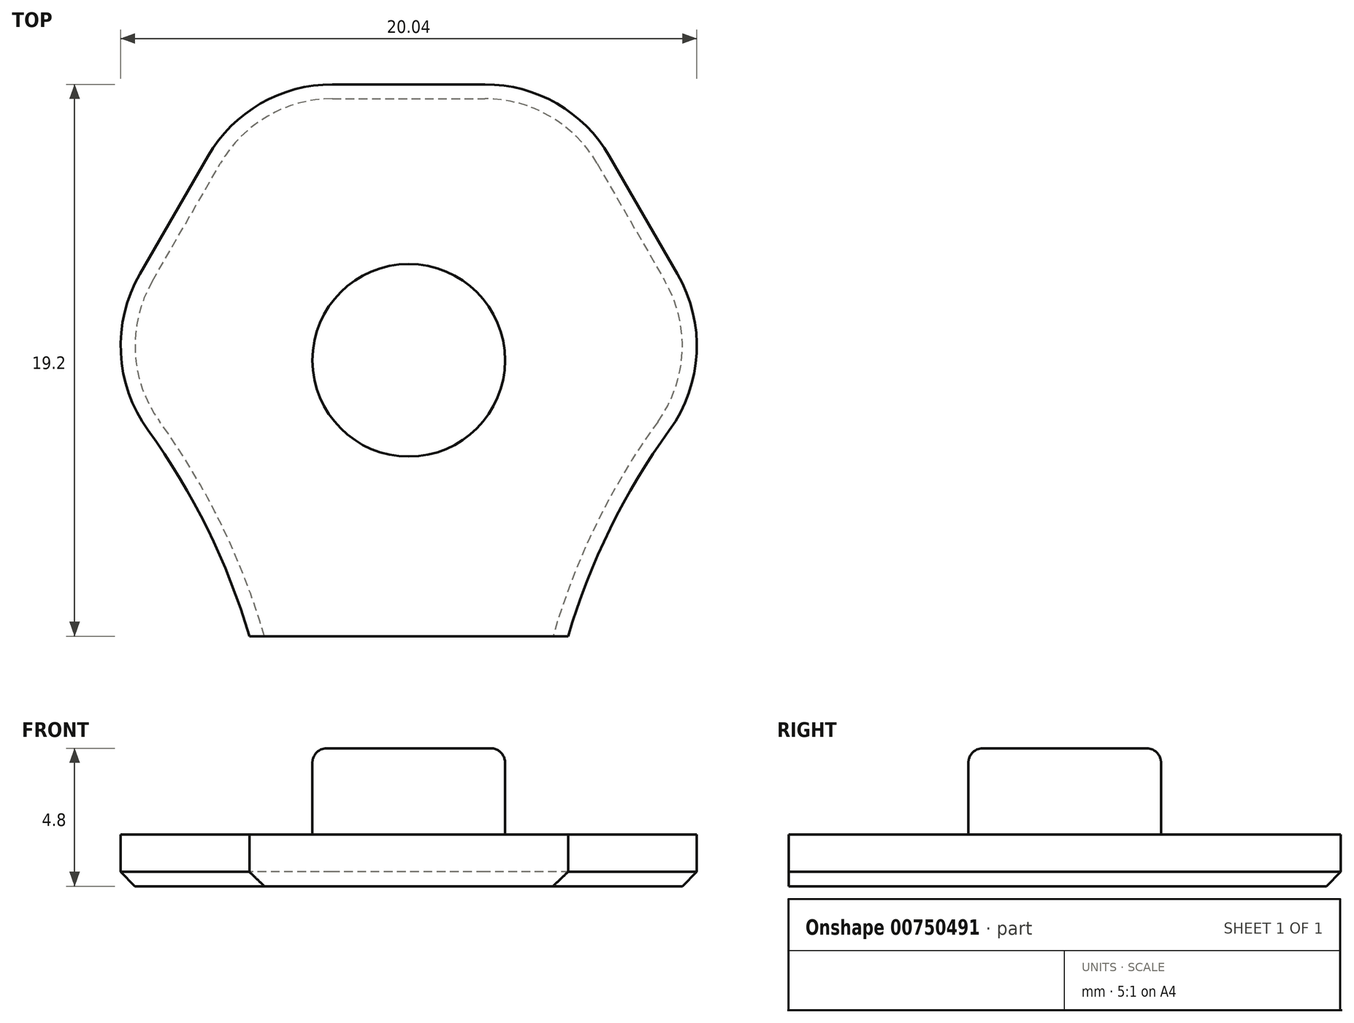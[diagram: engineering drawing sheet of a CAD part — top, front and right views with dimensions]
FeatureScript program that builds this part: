
annotation { "Feature Type Name" : "Feature", "Feature Type Description" : "" }
export const myFeature = defineFeature(function(context is Context, id is Id, definition is map)
    precondition{}
    {
        {
            var Q0;
            Q0=qCreatedBy(makeId("Top.planeOp"),FACE);
            var sketch = newSketch(context, id + "F0", { "sketchPlane" : qUnion([Q0])});
            skCircle(sketch, "E0.cCircle", {"center": v(0, 0) * mm, "radius": 6.4 * mm, "construction": true});
            skLineSegment(sketch, "E0.0", {"start": v(3.7, -6.4) * mm, "end": v(-3.7, -6.4) * mm});
            skLineSegment(sketch, "E0.1", {"start": v(-3.7, -6.4) * mm, "end": v(-7.4, 0) * mm});
            skLineSegment(sketch, "E0.2", {"start": v(-7.4, 0) * mm, "end": v(-3.7, 6.4) * mm});
            skLineSegment(sketch, "E0.3", {"start": v(-3.7, 6.4) * mm, "end": v(3.7, 6.4) * mm});
            skLineSegment(sketch, "E0.4", {"start": v(3.7, 6.4) * mm, "end": v(7.4, 0) * mm});
            skLineSegment(sketch, "E0.5", {"start": v(7.4, 0) * mm, "end": v(3.7, -6.4) * mm});
            skPoint(sketch, "E0.0.midPoint", {"position": v(0, -6.4) * mm});
            skCircle(sketch, "E1.cCircle", {"center": v(0, 0) * mm, "radius": 9.6 * mm, "construction": true});
            skLineSegment(sketch, "E1.1", {"start": v(5.54, -9.6) * mm, "end": v(-5.54, -9.6) * mm});
            skLineSegment(sketch, "E1.3", {"start": v(-11.09, 0) * mm, "end": v(-5.54, 9.6) * mm});
            skLineSegment(sketch, "E1.4", {"start": v(-5.54, 9.6) * mm, "end": v(5.54, 9.6) * mm});
            skLineSegment(sketch, "E1.5", {"start": v(5.54, 9.6) * mm, "end": v(11.09, 0) * mm});
            skPoint(sketch, "E1.0.midPoint", {"position": v(8.31, -4.8) * mm});
            skArc(sketch, "E2", {"start": v(-5.54, -9.6) * mm, "mid": v(-7.75, -4.47) * mm, "end": v(-11.09, 0) * mm});
            skArc(sketch, "E3", {"start": v(11.09, 0) * mm, "mid": v(7.75, -4.47) * mm, "end": v(5.54, -9.6) * mm});
            skCircle(sketch, "E4", {"center": v(0, 0) * mm, "radius": 3.35 * mm});
            skSolve(sketch);
        }
        {
            var Q0;
            Q0=makeQuery(id+"F0.imprint","IMPRINT",FACE,{"disambiguationData":[TD([[makeQuery(id+"F0.imprint","IMPRINT",EDGE,{"derivedFrom":sQuery(id+"F0.wireOp",EDGE,"E0.0")}),1.0]])]});
            var Q1;
            Q1=makeQuery(id+"F0.imprint","IMPRINT",FACE,{"disambiguationData":[TD([[makeQuery(id+"F0.imprint","IMPRINT",EDGE,{"derivedFrom":sQuery(id+"F0.wireOp",EDGE,"E0.0")}),-1.0]])]});
            extrude(context, id + "F1", {"entities" : qUnion([Q0, Q1]), "depth" : 1.8 * mm, "offsetDistance" : 25 * mm});
        }
        {
            var Q0;
            Q0=makeQuery(id+"F1.opExtrude","SWEPT_EDGE",EDGE,{"disambiguationData":[OSD([sQuery(id+"F0.wireOp",EDGE,"E1.3"),sQuery(id+"F0.wireOp",EDGE,"E2")])]});
            var Q1;
            Q1=makeQuery(id+"F1.opExtrude","SWEPT_EDGE",EDGE,{"disambiguationData":[OSD([sQuery(id+"F0.wireOp",EDGE,"E1.3"),sQuery(id+"F0.wireOp",EDGE,"E1.4")])]});
            var Q2;
            Q2=makeQuery(id+"F1.opExtrude","SWEPT_EDGE",EDGE,{"disambiguationData":[OSD([sQuery(id+"F0.wireOp",EDGE,"E1.4"),sQuery(id+"F0.wireOp",EDGE,"E1.5")])]});
            var Q3;
            Q3=makeQuery(id+"F1.opExtrude","SWEPT_EDGE",EDGE,{"disambiguationData":[OSD([sQuery(id+"F0.wireOp",EDGE,"E1.5"),sQuery(id+"F0.wireOp",EDGE,"E3")])]});
            fillet(context, id + "F2", {"entities" : qUnion([Q0, Q1, Q2, Q3]), "radius" : 5 * mm, "tangentPropagation" : true, "allowEdgeOverflow" : false});
        }
        {
            var Q0;
            Q0=makeQuery(id+"F0.imprint","IMPRINT",FACE,{"disambiguationData":[TD([[makeQuery(id+"F0.imprint","IMPRINT",EDGE,{"derivedFrom":sQuery(id+"F0.wireOp",EDGE,"E4")}),1.0]])]});
            extrude(context, id + "F3", {"entities" : qUnion([Q0]), "operationType" : NewBodyOperationType.ADD, "depth" : 4.8 * mm, "offsetDistance" : 25 * mm});
        }
        {
            var Q0;
            Q0=makeQuery(id+"F3.opExtrude","CAP_EDGE",EDGE,{"disambiguationData":[OSD([sQuery(id+"F0.wireOp",EDGE,"E4")])],"isStart":false});
            fillet(context, id + "F4", {"entities" : qUnion([Q0]), "radius" : 0.5 * mm, "tangentPropagation" : true, "allowEdgeOverflow" : false});
        }
        {
            var Q0;
            {var subQ0=sQuery(id+"F0.wireOp",EDGE,"E1.4");var subQ1=sQuery(id+"F0.wireOp",EDGE,"E1.3");Q0=makeQuery(id+"F2.opFillet","BLEND_EDGE",EDGE,{"blendedFrom":[makeQuery(id+"F1.opExtrude","SWEPT_EDGE",EDGE,{"disambiguationData":[OSD([subQ1,subQ0])]}),makeQuery(id+"F1.opExtrude","CAP_FACE",FACE,{"disambiguationData":[OSD([sQuery(id+"F0.wireOp",EDGE,"E1.1"),subQ1,subQ0,sQuery(id+"F0.wireOp",EDGE,"E1.5"),sQuery(id+"F0.wireOp",EDGE,"E2"),sQuery(id+"F0.wireOp",EDGE,"E3"),sQuery(id+"F0.wireOp",EDGE,"E4")])],"isStart":true})],"blendedInto":[makeQuery(id+"F1.opExtrude","CAP_FACE",FACE,{"disambiguationData":[OSD([sQuery(id+"F0.wireOp",EDGE,"E1.1"),subQ1,subQ0,sQuery(id+"F0.wireOp",EDGE,"E1.5"),sQuery(id+"F0.wireOp",EDGE,"E2"),sQuery(id+"F0.wireOp",EDGE,"E3"),sQuery(id+"F0.wireOp",EDGE,"E4")])],"isStart":true})]});}
            chamfer(context, id + "F5", {"entities" : qUnion([Q0]), "width" : 0.5 * mm, "tangentPropagation" : true});
        }
    });
